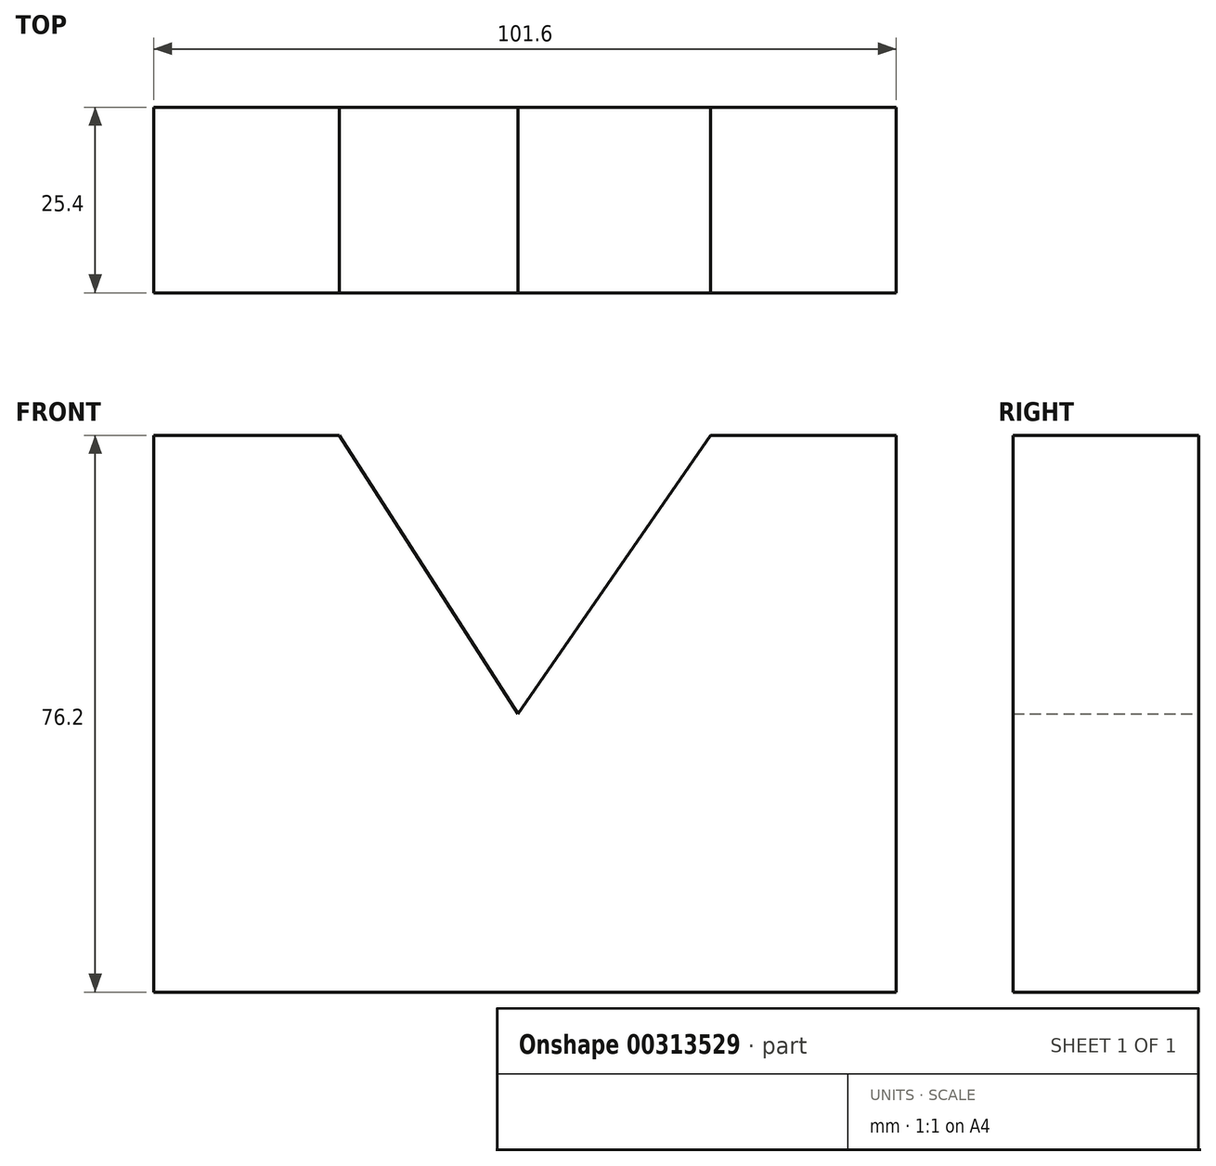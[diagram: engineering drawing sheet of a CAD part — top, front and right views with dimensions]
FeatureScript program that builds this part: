
annotation { "Feature Type Name" : "Feature", "Feature Type Description" : "" }
export const myFeature = defineFeature(function(context is Context, id is Id, definition is map)
    precondition{}
    {
        {
            var Q0;
            Q0=qCreatedBy(makeId("Front.planeOp"),FACE);
            var sketch = newSketch(context, id + "F0", { "sketchPlane" : qUnion([Q0])});
            skLineSegment(sketch, "E0", {"start": v(-43.3, 14.26) * mm, "end": v(-43.3, -61.94) * mm});
            skLineSegment(sketch, "E1", {"start": v(-43.3, -61.94) * mm, "end": v(58.3, -61.94) * mm});
            skLineSegment(sketch, "E2", {"start": v(58.3, -61.94) * mm, "end": v(58.3, 14.26) * mm});
            skLineSegment(sketch, "E3", {"start": v(58.3, 14.26) * mm, "end": v(32.9, 14.26) * mm});
            skLineSegment(sketch, "E4", {"start": v(32.9, 14.26) * mm, "end": v(6.57, -23.84) * mm});
            skLineSegment(sketch, "E5", {"start": v(6.57, -23.84) * mm, "end": v(-17.9, 14.26) * mm});
            skLineSegment(sketch, "E6", {"start": v(-17.9, 14.26) * mm, "end": v(-43.3, 14.26) * mm});
            skSolve(sketch);
        }
        {
            var Q0;
            Q0=makeQuery(id+"F0.imprint","IMPRINT",FACE,{"disambiguationData":[TD([[makeQuery(id+"F0.imprint","IMPRINT",EDGE,{"derivedFrom":sQuery(id+"F0.wireOp",EDGE,"E0")}),1.0]])]});
            extrude(context, id + "F1", {"entities" : qUnion([Q0]), "depth" : 25.4 * mm});
        }
    });
